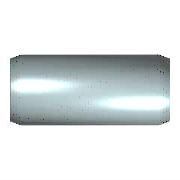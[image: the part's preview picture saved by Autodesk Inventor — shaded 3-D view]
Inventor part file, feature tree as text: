
AUTODESK INVENTOR PART (.ipt)
format: ipt  version: 2023.3 (Build 273359000, 359)  size: 113,664 bytes
history: native  units: mm (DEFAULTED — no unit token found)
features: extrude x1, chamfer x1, sketch x1
ambient origin geometry x8: Origin, YZ Plane, XZ Plane, XY Plane, X Axis, Y Axis, Z Axis, Center Point
bodies: Solid1 (feature_tree)
feature tree (3):
  extrude  "Körper"  Depth=18.0mm
  chamfer  "Skizze2"  [1 undecoded]
  sketch  "Skizze"  dims[d1=2.0mm d2=18.0mm d3=0.0mm d4=0.35mm d5=15.0deg d8=0.35mm d9=15.0deg d11=0.35mm d12=0.35mm d13=0.0mm d15=0.0mm d16=0.0mm]
note: 1 required parameter value undecoded (feature->parameter linkage not recoverable at this tier; creation-order binding heuristic only, values carry confidence <= 0.55)
